# Revit family: VL1GL1501xWSxx
name_source: partatom
category: Leuchten
units: mm (PartAtom-declared; Revit-internal decimal feet)

## family parameters
Basisbauteil = Fläche
Beim Laden mit Abzugskörper schneiden = Nein
Bemaßung runder Anschluss = Durchmesser verwenden
Gemeinsam genutzt = Nein
Lichtquelle = Ja
OmniClass-Nummer = 23.80.70.11
OmniClass-Titel = Luminaries for Internal Lighting
Raumberechnungspunkt = Nein
Teiletyp = Normal

## types (12) — shared parameters
Baugruppenkennzeichen = D5020200
Emissionsform beim Rendern sichtbar = Nein
Farbfilter = 16777215
Farbtemperaturverschiebung bei Dämpfen der Lampe = <Keine Auswahl>
Hersteller = RIDI Leuchten GmbH
Lampe = LED
Neigungswinkel = 90.00°
URL = www.ridi.de
Von Breite des Rechtecks ausssenden = 1479 mm  [stored 4.85236 ft]
Von Länge des Rechtecks aussenden = 61 mm  [stored 0.200131 ft]
brand = RIDI
conformity mark = CE
electrical safety class = 1
height = 61 mm  [stored 0.200131 ft]
ingress protection (IP) code = IP20
length = 1500 mm  [stored 4.92126 ft]
nominal frequency = 50-60Hz
nominal voltage = 230
voltage type (AC, DC, UC) = AC
width = 67 mm
zero-valued in all types: Vorgabe-Ansicht

## per-type parameters (varying)
| type | Datei für fotometrisches Netz | Modell | Scheinlast | rated input power | weight |
| VL1GL1501-5NDWS840BU0700 | VL1GL1501_B.IES | 1552000 | 41 VA | 41 | 1,7kg |
| VL1GL1501-5NDWS840E0800 | VL1GL1501_E.IES | 1552001 | 48 VA | 48 | 1,7kg |
| VL1GL1501-7DAWS840BU0700 | VL1GL1501_B.IES | 1562000 | 40 VA | 40 | 1,7kg |
| VL1GL1501-7DAWS840E0800 | VL1GL1501_E.IES | 1562001 | 47 VA | 47 | 1,7kg |
| VL1GL1501-5FLWS840BE1500 | Master_VL2P-GL150-5FLWS840BE1500.IES | 1552014 | 84 VA | 84 | 2,43kg |
| VL1GL1501-5FLWS865BE1500 | Master_VL2P-GL150-5FLWS840BE1500.IES | 1552017 | 84 VA | 84 | 2,43kg |
| VL1GL1501-7DAWS840BE1500 | Master_VL2P-GL150-5FLWS840BE1500.IES | 1562014 | 85 VA | 85 | 2,43kg |
| VL1GL1501-7DAWS865BE1500 | Master_VL2P-GL150-5FLWS840BE1500.IES | 1562017 | 85 VA | 85 | 2,43kg |
| VL1GL1501-5FLWS840B1500 | Master_VLxx-GLxxxB_IP20.IES | 1552027 | 84 VA | 84 | 2,43kg |
| VL1GL1501-5FLWS865B1500 | Master_VLxx-GLxxxB_IP20.IES | 1552029 | 84 VA | 84 | 2,43kg |
| VL1GL1501-7DAWS840B1500 | Master_VLxx-GLxxxB_IP20.IES | 1562027 | 85 VA | 85 | 2,43kg |
| VL1GL1501-7DAWS865B1500 | Master_VLxx-GLxxxB_IP20.IES | 1562029 | 84 VA | 84 | 2,43kg |

note: column(s) folded — value = type name in every type: product name

note: [stored X ft] marks values corroborated as IEEE doubles in the binary element streams (Revit-internal decimal feet)
